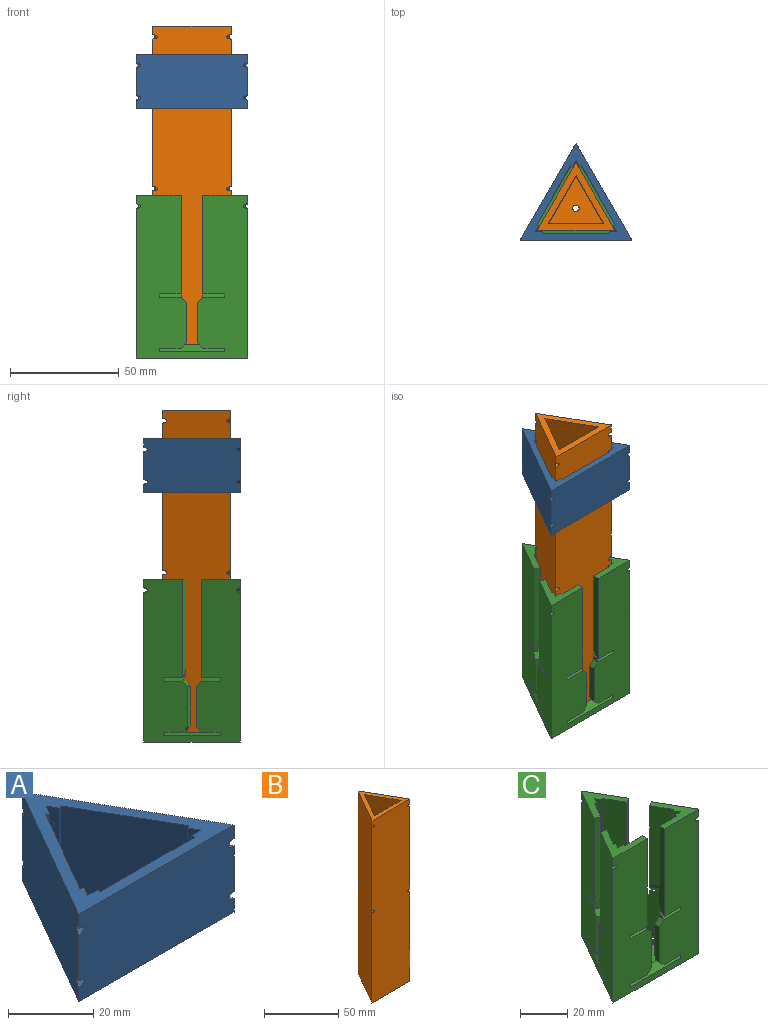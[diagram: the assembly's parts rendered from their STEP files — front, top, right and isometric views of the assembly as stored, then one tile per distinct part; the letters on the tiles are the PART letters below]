
ASSEMBLY  parts=3 mates=5
PART A: 26 faces, bbox 52.4x45.4x25 mm
  f0: plane 31x25mm, normal (0,1,0), area 775mm2, adj f6,f7,f15,f16
  f1: plane 26.85x25mm, normal (-0.87,-0.5,0), area 775mm2, adj f6,f7,f11,f12
  f2: plane 26.85x25mm, normal (0.87,-0.5,0), area 775mm2, adj f6,f7,f8,f19
  f3: plane 44.51x25.7mm, normal (0.87,0.5,0), area 1272.2mm2, adj f4,f5,f6,f7,f20,f21,f22,f23
  f4: plane 44.51x25.7mm, normal (-0.87,0.5,0), area 1272.2mm2, adj f3,f5,f6,f7,f20,f21,f24,f25
  f5: plane 51.39x25mm, normal (0,-1,0), area 1272.2mm2, adj f3,f4,f6,f7,f22,f23,f24,f25
  f6: plane 51.39x44.51mm, normal (0,0,1), area 440.6mm2, adj f0,f1,f2,f3,f4,f5,f8,f9
  f7: plane 51.39x44.51mm, normal (0,0,-1), area 440.6mm2, adj f0,f1,f2,f3,f4,f5,f8,f9
  f8: plane 25x0.87mm, normal (-0.5,-0.87,0), area 25mm2, adj f2,f6,f7,f9
  f9: plane 25x2.83mm, normal (0.87,-0.5,0), area 75.4mm2, adj f6,f7,f8,f10,f20,f21
  f10: plane 25x2.83mm, normal (-0.87,-0.5,0), area 75.4mm2, adj f6,f7,f9,f11,f20,f21
  f11: plane 25x0.87mm, normal (0.5,-0.87,0), area 25mm2, adj f1,f6,f7,f10
  f12: plane 25x0.87mm, normal (-0.5,0.87,0), area 25mm2, adj f1,f6,f7,f13
  f13: plane 25x2.83mm, normal (-0.87,-0.5,0), area 75.4mm2, adj f6,f7,f12,f14,f22,f23
  f14: plane 25x3.27mm, normal (0,1,0), area 75.4mm2, adj f6,f7,f13,f15,f22,f23
  f15: plane 25x1mm, normal (-1,0,0), area 25mm2, adj f0,f6,f7,f14
  f16: plane 25x1mm, normal (1,0,0), area 25mm2, adj f0,f6,f7,f17
  f17: plane 25x3.27mm, normal (0,1,0), area 75.4mm2, adj f6,f7,f16,f18,f24,f25
  f18: plane 25x2.83mm, normal (0.87,-0.5,0), area 75.4mm2, adj f6,f7,f17,f19,f24,f25
  f19: plane 25x0.87mm, normal (0.5,0.87,0), area 25mm2, adj f2,f6,f7,f18
  f20: cylinder r=1mm len=9.74mm, axis (0,-1,0), area 50.3mm2, adj f3,f4,f9,f10
  f21: cylinder r=1mm len=9.74mm, axis (0,-1,0), area 50.3mm2, adj f3,f4,f9,f10
  f22: cylinder r=1mm len=9.43mm, axis (-0.87,0.5,0), area 50.3mm2, adj f3,f5,f13,f14
  f23: cylinder r=1mm len=9.43mm, axis (-0.87,0.5,0), area 50.3mm2, adj f3,f5,f13,f14
  f24: cylinder r=1mm len=9.43mm, axis (0.87,0.5,0), area 50.3mm2, adj f4,f5,f17,f18
  f25: cylinder r=1mm len=9.43mm, axis (0.87,0.5,0), area 50.3mm2, adj f4,f5,f17,f18
PART B: 16 faces, bbox 37x32x150 mm
  f0: plane 147x22.18mm, normal (0.87,-0.5,0), area 3751.8mm2, adj f1,f2,f6,f8,f10,f11,f12,f13
  f1: plane 147x22.18mm, normal (-0.87,-0.5,0), area 3751.8mm2, adj f0,f2,f6,f8,f10,f11,f14,f15
  f2: plane 147x25.61mm, normal (0,1,0), area 3751.8mm2, adj f0,f1,f6,f8,f12,f13,f14,f15
  f3: plane 150x36mm, normal (0,-1,0), area 5387.4mm2, adj f4,f5,f6,f7,f12,f13,f14,f15
  f4: plane 150x31.18mm, normal (0.87,0.5,0), area 5387.4mm2, adj f3,f5,f6,f7,f10,f11,f14,f15
  f5: plane 150x31.18mm, normal (-0.87,0.5,0), area 5387.4mm2, adj f3,f4,f6,f7,f10,f11,f12,f13
  f6: plane 36x31.18mm, normal (0,0,1), area 277.2mm2, adj f0,f1,f2,f3,f4,f5
  f7: plane 36x31.18mm, normal (0,0,-1), area 554.1mm2, adj f3,f4,f5,f9
  f8: plane 25.61x22.18mm, normal (0,0,1), area 276.9mm2, adj f0,f1,f2,f9
  f9: cylinder r=1.5mm len=3mm, axis (0,0,-1), area 28.3mm2, adj f7,f8
  f10: cylinder r=1mm len=7.74mm, axis (0,-1,0), area 37.7mm2, adj f0,f1,f4,f5
  f11: cylinder r=1mm len=7.74mm, axis (0,-1,0), area 37.7mm2, adj f0,f1,f4,f5
  f12: cylinder r=1mm len=7.7mm, axis (0.87,0.5,0), area 37.7mm2, adj f0,f2,f3,f5
  f13: cylinder r=1mm len=7.7mm, axis (0.87,0.5,0), area 37.7mm2, adj f0,f2,f3,f5
  f14: cylinder r=1mm len=7.7mm, axis (-0.87,0.5,0), area 37.7mm2, adj f1,f2,f3,f4
  f15: cylinder r=1mm len=7.7mm, axis (-0.87,0.5,0), area 37.7mm2, adj f1,f2,f3,f4
PART C: 108 faces, bbox 52.4x45.4x75 mm
  f0: plane 72x26.85mm, normal (0.87,-0.5,0), area 1472.3mm2, adj f1,f4,f6,f8,f10,f11,f26,f29
  f1: plane 27.48x17.6mm, normal (-0.61,0.35,0.71), area 109.2mm2, adj f0,f5,f81,f82,f102,f103,f104
  f2: plane 72x26.85mm, normal (-0.87,-0.5,0), area 1472.3mm2, adj f3,f11,f13,f15,f17,f18,f26,f32
  f3: plane 27.48x17.6mm, normal (0.61,0.35,0.71), area 109.2mm2, adj f2,f12,f62,f63,f99,f100,f101
  f4: plane 20.7x17.92mm, normal (0,0,1), area 116.9mm2, adj f0,f5,f19,f20,f33,f34,f35,f36
  f5: plane 75x44.51mm, normal (-0.87,0.5,0), area 3173.1mm2, adj f1,f4,f6,f7,f9,f11,f12,f20
  f6: plane 10.16x7.6mm, normal (-0.61,0.35,0.71), area 42.4mm2, adj f0,f5,f86,f98
  f7: plane 9.43x6.33mm, normal (0.61,-0.35,-0.71), area 21.7mm2, adj f5,f8,f86,f96
  f8: cylinder r=5mm len=9.39mm, axis (-0.5,-0.87,0), area 39.3mm2, adj f0,f7,f86,f96
  f9: plane 9.99x7.1mm, normal (0.61,-0.35,-0.71), area 23.4mm2, adj f5,f10,f82,f89
  f10: cylinder r=5mm len=11.56mm, axis (-0.5,-0.87,0), area 48.5mm2, adj f0,f9,f82,f89,f90
  f11: plane 20.7x19.42mm, normal (0,0,1), area 116.9mm2, adj f0,f2,f5,f12,f29,f30,f31,f32
  f12: plane 75x44.51mm, normal (0.87,0.5,0), area 3173.1mm2, adj f3,f5,f11,f13,f14,f16,f18,f20
  f13: plane 10.16x7.6mm, normal (0.61,0.35,0.71), area 42.4mm2, adj f2,f12,f67,f79
  f14: plane 9.43x6.33mm, normal (-0.61,-0.35,-0.71), area 21.7mm2, adj f12,f15,f67,f77
  f15: cylinder r=5mm len=9.39mm, axis (-0.5,0.87,0), area 39.3mm2, adj f2,f14,f67,f77
  f16: plane 10.76x6.33mm, normal (-0.61,-0.35,-0.71), area 23.4mm2, adj f12,f17,f63,f70
  f17: cylinder r=5mm len=11.56mm, axis (-0.5,0.87,0), area 48.5mm2, adj f2,f16,f63,f70,f71
  f18: plane 20.7x17.92mm, normal (0,0,1), area 116.9mm2, adj f2,f12,f19,f20,f37,f38,f39,f40
  f19: plane 72x31mm, normal (0,1,0), area 1485.1mm2, adj f4,f18,f21,f23,f25,f26,f33,f40
  f20: plane 75x51.39mm, normal (0,-1,0), area 3173.1mm2, adj f4,f5,f12,f18,f21,f22,f24,f27
  f21: plane 10x3mm, normal (0,-0.71,0.71), area 42.4mm2, adj f19,f20,f48,f60
  f22: plane 10x1.54mm, normal (0,0.71,-0.71), area 21.7mm2, adj f20,f23,f48,f58
  f23: cylinder r=5mm len=10mm, axis (1,0,0), area 39.3mm2, adj f19,f22,f48,f58
  f24: plane 11.54x1.54mm, normal (0,0.71,-0.71), area 23.4mm2, adj f20,f25,f44,f51
  f25: cylinder r=5mm len=12.5mm, axis (1,0,0), area 48.5mm2, adj f19,f24,f44,f51,f52
  f26: plane 37.54x33.51mm, normal (0,0,1), area 696mm2, adj f0,f2,f19,f28,f29,f30,f31,f32
  f27: plane 51.39x44.51mm, normal (0,0,-1), area 1136.6mm2, adj f5,f12,f20,f28
  f28: cylinder r=1.5mm len=3mm, axis (0,0,-1), area 28.3mm2, adj f26,f27
  f29: plane 72x0.87mm, normal (-0.5,-0.87,0), area 72mm2, adj f0,f11,f26,f30
  f30: plane 72x2.83mm, normal (0.87,-0.5,0), area 232.2mm2, adj f11,f26,f29,f31,f105
  f31: plane 72x2.83mm, normal (-0.87,-0.5,0), area 232.2mm2, adj f11,f26,f30,f32,f105
  f32: plane 72x0.87mm, normal (0.5,-0.87,0), area 72mm2, adj f2,f11,f26,f31
  f33: plane 72x1mm, normal (1,0,0), area 72mm2, adj f4,f19,f26,f34
  f34: plane 72x3.27mm, normal (0,1,0), area 232.2mm2, adj f4,f26,f33,f35,f106
  f35: plane 72x2.83mm, normal (0.87,-0.5,0), area 232.2mm2, adj f4,f26,f34,f36,f106
  f36: plane 72x0.87mm, normal (0.5,0.87,0), area 72mm2, adj f0,f4,f26,f35
  f37: plane 72x0.87mm, normal (-0.5,0.87,0), area 72mm2, adj f2,f18,f26,f38
  f38: plane 72x2.83mm, normal (-0.87,-0.5,0), area 232.2mm2, adj f18,f26,f37,f39,f107
  f39: plane 72x3.27mm, normal (0,1,0), area 232.2mm2, adj f18,f26,f38,f40,f107
  f40: plane 72x1mm, normal (-1,0,0), area 72mm2, adj f18,f19,f26,f39
  f41: plane 30x3mm, normal (0,-0.71,0.71), area 127.3mm2, adj f19,f20,f43,f44
  f42: plane 11.54x1.54mm, normal (0,0.71,-0.71), area 23.4mm2, adj f20,f43,f45,f56
  f43: plane 6.57x3mm, normal (1,0,0), area 5mm2, adj f19,f20,f41,f42,f45
  f44: plane 6.57x3mm, normal (-1,0,0), area 5mm2, adj f19,f20,f24,f25,f41
  f45: cylinder r=5mm len=12.5mm, axis (1,0,0), area 48.5mm2, adj f19,f42,f43,f55,f56
  f46: plane 10x3mm, normal (0,-0.71,0.71), area 42.4mm2, adj f19,f20,f49,f59
  f47: plane 10x1.54mm, normal (0,0.71,-0.71), area 21.7mm2, adj f20,f49,f50,f57
  f48: plane 6.57x3mm, normal (1,0,0), area 5mm2, adj f19,f20,f21,f22,f23
  f49: plane 6.57x3mm, normal (-1,0,0), area 5mm2, adj f19,f20,f46,f47,f50
  f50: cylinder r=5mm len=10mm, axis (1,0,0), area 39.3mm2, adj f19,f47,f49,f57
  f51: plane 2.5x2.5mm, normal (-0.71,0,-0.71), area 4.3mm2, adj f20,f24,f25,f52
  f52: plane 18.5x3mm, normal (-1,0,0), area 54.9mm2, adj f19,f20,f25,f51,f54
  f53: plane 3x2.5mm, normal (0.71,0,0.71), area 10.6mm2, adj f19,f20,f55,f60
  f54: plane 3x2.5mm, normal (-0.71,0,0.71), area 10.6mm2, adj f19,f20,f52,f59
  f55: plane 18.5x3mm, normal (1,0,0), area 54.9mm2, adj f19,f20,f45,f53,f56
  f56: plane 2.5x2.5mm, normal (0.71,0,-0.71), area 4.3mm2, adj f20,f42,f45,f55
  f57: plane 45.5x3mm, normal (-1,0,0), area 131.5mm2, adj f18,f19,f20,f47,f50
  f58: plane 45.5x3mm, normal (1,0,0), area 131.5mm2, adj f4,f19,f20,f22,f23
  f59: plane 3x3mm, normal (-1,0,0), area 4.5mm2, adj f19,f46,f54
  f60: plane 3x3mm, normal (1,0,0), area 4.5mm2, adj f19,f21,f53
  f61: plane 9.99x7.1mm, normal (-0.61,-0.35,-0.71), area 23.4mm2, adj f12,f62,f64,f75
  f62: plane 6.57x2.6mm, normal (-0.5,0.87,0), area 5mm2, adj f2,f3,f12,f61,f64
  f63: plane 6.57x2.6mm, normal (0.5,-0.87,0), area 5mm2, adj f2,f3,f12,f16,f17
  f64: cylinder r=5mm len=11.56mm, axis (-0.5,0.87,0), area 48.5mm2, adj f2,f61,f62,f74,f75
  f65: plane 10.16x7.6mm, normal (0.61,0.35,0.71), area 42.4mm2, adj f2,f12,f68,f78
  f66: plane 9.43x6.33mm, normal (-0.61,-0.35,-0.71), area 21.7mm2, adj f12,f68,f69,f76
  f67: plane 6.57x2.6mm, normal (-0.5,0.87,0), area 5mm2, adj f2,f12,f13,f14,f15
  f68: plane 6.57x2.6mm, normal (0.5,-0.87,0), area 5mm2, adj f2,f12,f65,f66,f69
  f69: cylinder r=5mm len=9.39mm, axis (-0.5,0.87,0), area 39.3mm2, adj f2,f66,f68,f76
  f70: plane 3.31x2.5mm, normal (0.35,-0.61,-0.71), area 4.3mm2, adj f12,f16,f17,f71
  f71: plane 18.5x2.6mm, normal (0.5,-0.87,0), area 54.9mm2, adj f2,f12,f17,f70,f73
  f72: plane 3.85x3.67mm, normal (-0.35,0.61,0.71), area 10.6mm2, adj f2,f12,f74,f79
  f73: plane 3.85x3.67mm, normal (0.35,-0.61,0.71), area 10.6mm2, adj f2,f12,f71,f78
  f74: plane 18.5x2.6mm, normal (-0.5,0.87,0), area 54.9mm2, adj f2,f12,f64,f72,f75
  f75: plane 3.23x2.5mm, normal (-0.35,0.61,-0.71), area 4.3mm2, adj f12,f61,f64,f74
  f76: plane 45.5x2.6mm, normal (0.5,-0.87,0), area 131.5mm2, adj f2,f11,f12,f66,f69
  f77: plane 45.5x2.6mm, normal (-0.5,0.87,0), area 131.5mm2, adj f2,f12,f14,f15,f18
  f78: plane 3x2.6mm, normal (0.5,-0.87,0), area 4.5mm2, adj f2,f65,f73
  f79: plane 3x2.6mm, normal (-0.5,0.87,0), area 4.5mm2, adj f2,f13,f72
  f80: plane 10.76x6.33mm, normal (0.61,-0.35,-0.71), area 23.4mm2, adj f5,f81,f83,f94
  f81: plane 6.57x2.6mm, normal (-0.5,-0.87,0), area 5mm2, adj f0,f1,f5,f80,f83
  f82: plane 6.57x2.6mm, normal (0.5,0.87,0), area 5mm2, adj f0,f1,f5,f9,f10
  f83: cylinder r=5mm len=11.56mm, axis (-0.5,-0.87,0), area 48.5mm2, adj f0,f80,f81,f93,f94
  f84: plane 10.16x7.6mm, normal (-0.61,0.35,0.71), area 42.4mm2, adj f0,f5,f87,f97
  f85: plane 9.43x6.33mm, normal (0.61,-0.35,-0.71), area 21.7mm2, adj f5,f87,f88,f95
  f86: plane 6.57x2.6mm, normal (-0.5,-0.87,0), area 5mm2, adj f0,f5,f6,f7,f8
  f87: plane 6.57x2.6mm, normal (0.5,0.87,0), area 5mm2, adj f0,f5,f84,f85,f88
  f88: cylinder r=5mm len=9.39mm, axis (-0.5,-0.87,0), area 39.3mm2, adj f0,f85,f87,f95
  f89: plane 3.23x2.5mm, normal (0.35,0.61,-0.71), area 4.3mm2, adj f5,f9,f10,f90
  f90: plane 18.5x2.6mm, normal (0.5,0.87,0), area 54.9mm2, adj f0,f5,f10,f89,f92
  f91: plane 3.85x3.67mm, normal (-0.35,-0.61,0.71), area 10.6mm2, adj f0,f5,f93,f98
  f92: plane 3.85x3.67mm, normal (0.35,0.61,0.71), area 10.6mm2, adj f0,f5,f90,f97
  f93: plane 18.5x2.6mm, normal (-0.5,-0.87,0), area 54.9mm2, adj f0,f5,f83,f91,f94
  f94: plane 3.31x2.5mm, normal (-0.35,-0.61,-0.71), area 4.3mm2, adj f5,f80,f83,f93
  f95: plane 45.5x2.6mm, normal (0.5,0.87,0), area 131.5mm2, adj f0,f4,f5,f85,f88
  f96: plane 45.5x2.6mm, normal (-0.5,-0.87,0), area 131.5mm2, adj f0,f5,f7,f8,f11
  f97: plane 3x2.6mm, normal (0.5,0.87,0), area 4.5mm2, adj f0,f84,f92
  f98: plane 3x2.6mm, normal (-0.5,-0.87,0), area 4.5mm2, adj f0,f6,f91
  f99: plane 9.41x6.3mm, normal (0,0,1), area 15mm2, adj f2,f3,f100,f101
  f100: plane 2.05x1.5mm, normal (-0.35,0.61,-0.71), area 1.6mm2, adj f2,f3,f99
  f101: plane 2.05x1.5mm, normal (0.35,-0.61,-0.71), area 1.6mm2, adj f2,f3,f99
  f102: plane 9.41x6.3mm, normal (0,0,1), area 15mm2, adj f0,f1,f103,f104
  f103: plane 2.05x1.5mm, normal (0.35,0.61,-0.71), area 1.6mm2, adj f0,f1,f102
  f104: plane 2.05x1.5mm, normal (-0.35,-0.61,-0.71), area 1.6mm2, adj f0,f1,f102
  f105: cylinder r=1mm len=9.74mm, axis (0,-1,0), area 50.3mm2, adj f5,f12,f30,f31
  f106: cylinder r=1mm len=9.43mm, axis (0.87,0.5,0), area 50.3mm2, adj f5,f20,f34,f35
  f107: cylinder r=1mm len=9.43mm, axis (-0.87,0.5,0), area 50.3mm2, adj f12,f20,f38,f39
PLACE A t=(24.98,15.07,137.98)mm
PLACE B t=(24.98,15.07,26.12)mm fixed
PLACE C t=(24.98,15.07,23.12)mm
MATE cylindrical B.f9 <-> C.f28  axis (0,0,1) through (24.98,15.07,29.12)mm
MATE planar A.f5 <-> C.f20  axis (0,-1,0) through (24.98,0.24,150.48)mm
MATE planar C.f12 <-> A.f3  axis (0.87,0.5,0) through (37.83,22.49,59.92)mm
MATE parallel C.f2 <-> B.f4  axis (-0.87,-0.5,0) through (35.23,20.99,62.31)mm
MATE planar B.f9 <-> C.f28  axis (0,0,-1) through (24.98,15.07,26.12)mm
